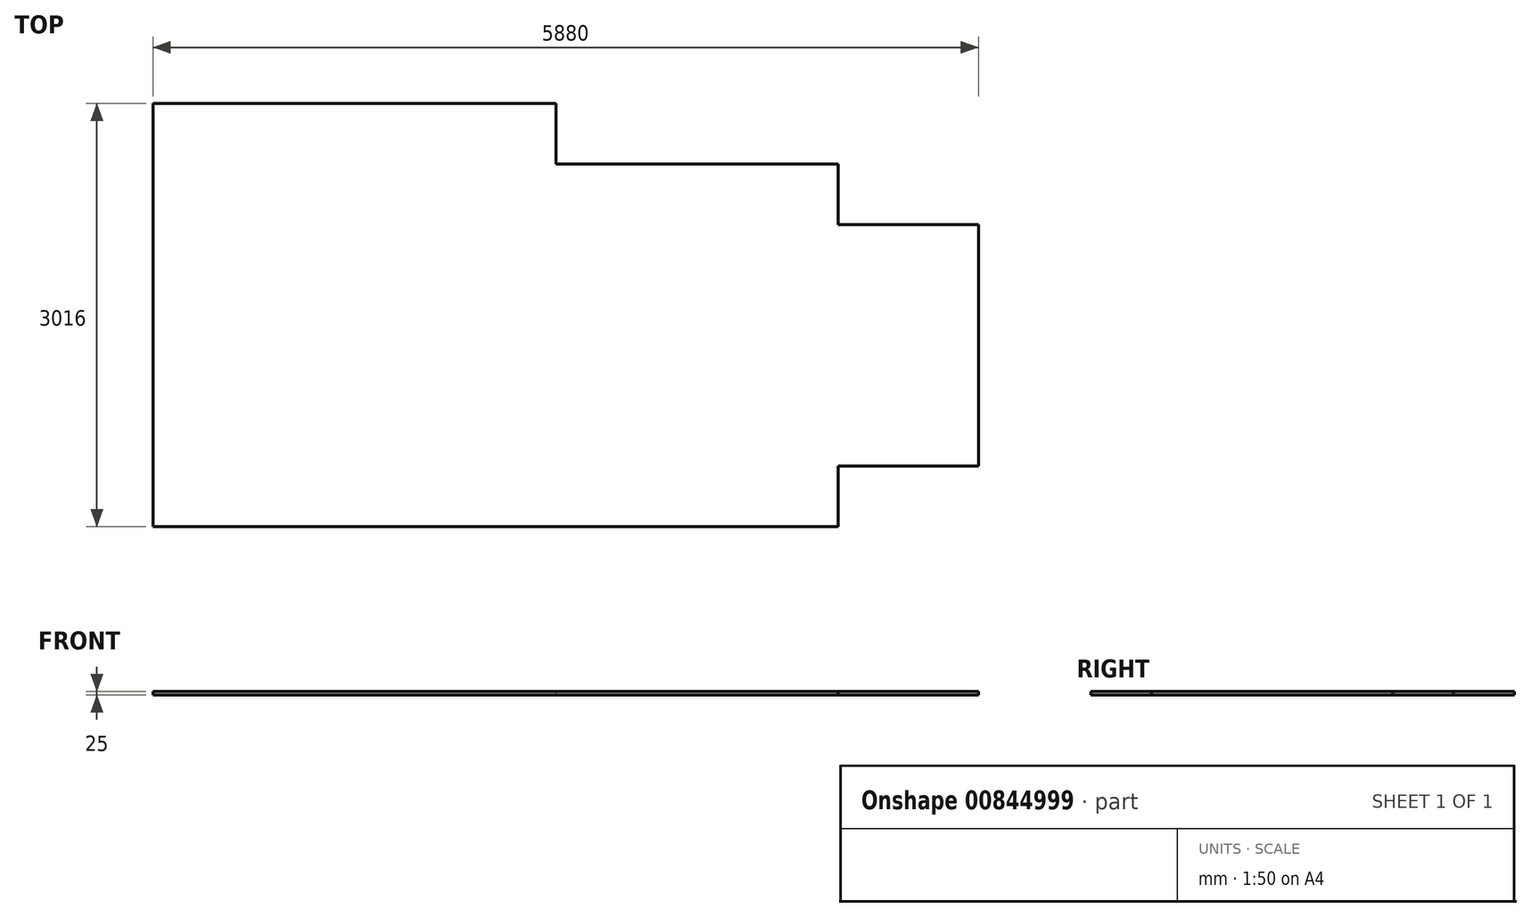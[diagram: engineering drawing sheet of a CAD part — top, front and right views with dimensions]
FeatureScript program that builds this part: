
annotation { "Feature Type Name" : "Feature", "Feature Type Description" : "" }
export const myFeature = defineFeature(function(context is Context, id is Id, definition is map)
    precondition{}
    {
        {
            var Q0;
            Q0=qCreatedBy(makeId("Top.planeOp"),FACE);
            var sketch = newSketch(context, id + "F0", { "sketchPlane" : qUnion([Q0])});
            skLineSegment(sketch, "E0", {"start": v(0, 0) * mm, "end": v(4880, 0) * mm});
            skLineSegment(sketch, "E1", {"start": v(4880, 0) * mm, "end": v(4880, 432) * mm});
            skLineSegment(sketch, "E2", {"start": v(4880, 432) * mm, "end": v(5880, 432) * mm});
            skLineSegment(sketch, "E3", {"start": v(5880, 432) * mm, "end": v(5880, 2152) * mm});
            skLineSegment(sketch, "E4", {"start": v(5880, 2152) * mm, "end": v(4880, 2152) * mm});
            skLineSegment(sketch, "E5", {"start": v(4880, 2152) * mm, "end": v(4880, 2584) * mm});
            skLineSegment(sketch, "E6", {"start": v(4880, 2584) * mm, "end": v(2872, 2584) * mm});
            skLineSegment(sketch, "E7", {"start": v(2872, 2584) * mm, "end": v(2872, 3016) * mm});
            skLineSegment(sketch, "E8", {"start": v(2872, 3016) * mm, "end": v(0, 3016) * mm});
            skLineSegment(sketch, "E9", {"start": v(0, 3016) * mm, "end": v(0, 0) * mm});
            skSolve(sketch);
        }
        {
            var Q0;
            Q0=qSketchRegion(id+"F0",true);
            extrude(context, id + "F1", {"entities" : qUnion([Q0]), "oppositeDirection" : true, "depth" : 25 * mm, "offsetDistance" : 25 * mm});
        }
    });
